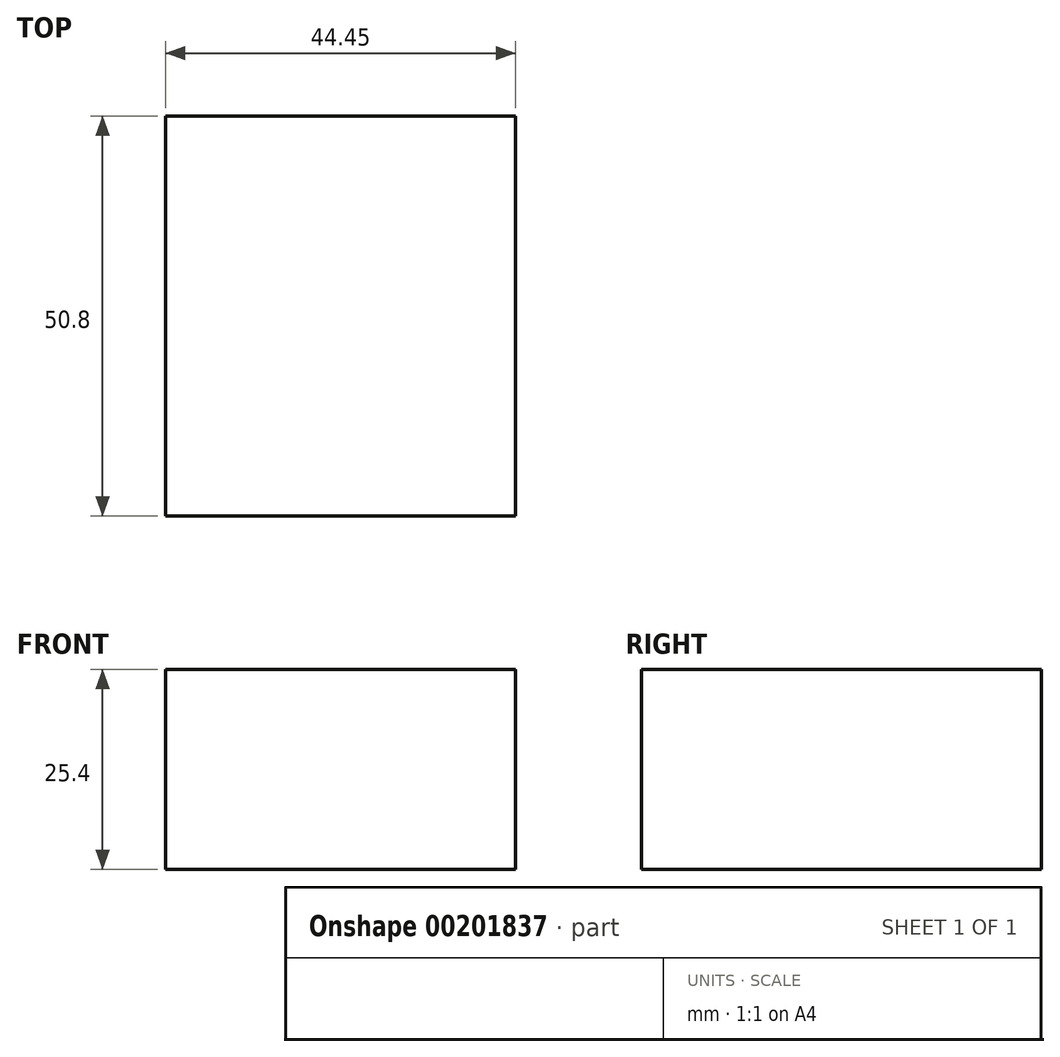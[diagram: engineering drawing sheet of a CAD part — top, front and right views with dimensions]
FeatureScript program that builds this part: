
annotation { "Feature Type Name" : "Feature", "Feature Type Description" : "" }
export const myFeature = defineFeature(function(context is Context, id is Id, definition is map)
    precondition{}
    {
        {
            var Q0;
            Q0=qCreatedBy(makeId("Top.planeOp"),FACE);
            var sketch = newSketch(context, id + "F0", { "sketchPlane" : qUnion([Q0])});
            skLineSegment(sketch, "E0.bottom", {"start": v(-27.44, 27.76) * mm, "end": v(17, 27.76) * mm});
            skLineSegment(sketch, "E0.top", {"start": v(-27.44, -23.04) * mm, "end": v(17, -23.04) * mm});
            skLineSegment(sketch, "E0.left", {"start": v(-27.44, 27.76) * mm, "end": v(-27.44, -23.04) * mm});
            skLineSegment(sketch, "E0.right", {"start": v(17, 27.76) * mm, "end": v(17, -23.04) * mm});
            skSolve(sketch);
        }
        {
            var Q0;
            Q0 = qSketchRegion(id + "F0", true);
            var Q1;
            Q1=makeQuery(id+"F0.imprint","IMPRINT",FACE,{"disambiguationData":[TD([[makeQuery(id+"F0.imprint","IMPRINT",EDGE,{"derivedFrom":sQuery(id+"F0.wireOp",EDGE,"E0.bottom")}),-1.0]])]});
            extrude(context, id + "F1", {"entities" : qUnion([Q0, Q1]), "depth" : 25.4 * mm});
        }
    });
